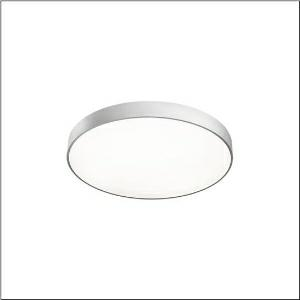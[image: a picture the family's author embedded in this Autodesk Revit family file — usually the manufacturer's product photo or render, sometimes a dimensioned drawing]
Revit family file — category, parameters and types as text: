
# Revit family: round_21_m_51mr36fm8421s
name_source: partatom
category: Lighting Fixtures
units: mm (PartAtom-declared; Revit-internal decimal feet)

## family parameters
Cut with Voids When Loaded = No
Host = Face
Light Source = No
Part Type = Normal
Room Calculation Point = No
Round Connector Dimension = Use Diameter
Shared = No

## types (1)
- --- (1 x LED, 8900 lm, 62.6 W, 4000K)
    Apparent Load = 63 VA
    CIE Flux Codes = 49 80 96 100 100
    Color Rendering = 80
    Color Temperature = 4000K
    Default Elevation = 1800 mm
    Description = Round 21 M, wall and ceiling luminaire, primary optical cover: cover, of PMMA, opal, light emission: direct distribution, primary light characteristic: symmetric, installation type: suspended mounting, surface-mounted, LED, rated luminous flux: 8.140lm, luminous efficacy: 133lm/W, light colour: 840, colour temperature: 4000K, control gear: ON/OFF Multilumen, with terminal, 3-pole, mains connection: 230V, AC, 50/60Hz, rated input power: 61W, housing, of aluminium, coated, silver, diameter: 600mm, height: 62mm, protection rating (complete): IP40, insulation class (complete): insulation class I (protective earthing), certification: CE, impact resistance: IK04, permissible operating ambient temperature: -10..+35°C, packaging unit: 1 piece
    Height = 87 mm
    Lamp = 1 x LED
    Lamp Light Flux = 8900 lm
    Lamp Power = 62.6 W
    Lamp count = 1
    Length = 600 mm
    Luminous efficacy = 142 lm/W
    Manufacturer = Siteco
    ModVariant = No
    Model = 51MR36FM8421S
    Mounting Place = Ceiling
    Mounting Type = Surface mounted
    Number of Poles = 1
    OnlyDefault = Yes
    Power Factor = 1
    Product Name = Round 21 M
    Product group = wall and ceiling luminaire
    ProductGroupID = 304
    Protection Class = Protection class I
    Protection Degree = IP 40
    RLX_Detail_Level = 1
    RLX_Emergency_Light_Flux = 0 lm
    RLX_Emergency_Type = 0
    RLX_Emergency_Type_DB = No
    RlxData = <blob elided: 17533 chars, md5=70b50105>
    Socket = socket
    Standby Power = 0 W
    System Light Flux = 8900 lm
    System Power = 63 W
    Type Comments = factory setting: luminous flux: 100 % | (ON | ON | ON | ON) | 700 mA
    Type Image = l_1258303.jpg
    URL = http://relux.com
    VarID = @adj_032846
    Voltage = 0 V
    Weight = 0.00 kg
    Width = 0 mm  [stored 0 ft]

note: [stored X ft] marks values corroborated as IEEE doubles in the binary element streams (Revit-internal decimal feet)

## geometry (parser evidence)
native form markers: Blend x4, Sweep x10
no freeform markers — native parametric forms only
